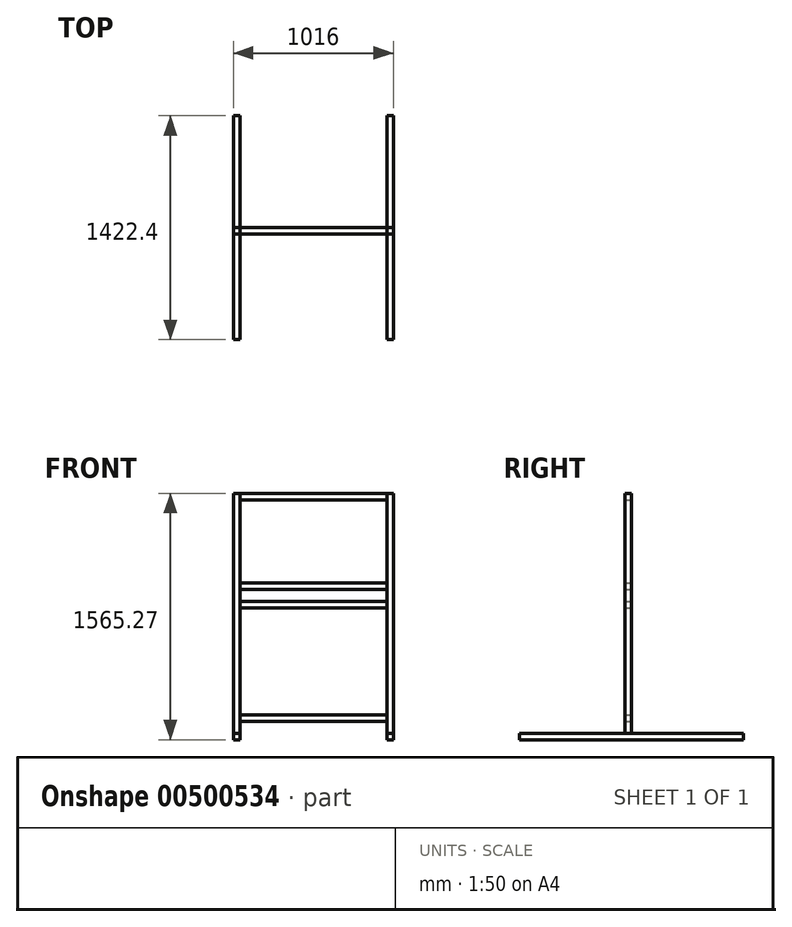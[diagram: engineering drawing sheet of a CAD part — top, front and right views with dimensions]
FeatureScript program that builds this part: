
annotation { "Feature Type Name" : "Feature", "Feature Type Description" : "" }
export const myFeature = defineFeature(function(context is Context, id is Id, definition is map)
    precondition{}
    {
        {
            var Q0;
            Q0=qCreatedBy(makeId("Front.planeOp"),FACE);
            var sketch = newSketch(context, id + "F0", { "sketchPlane" : qUnion([Q0])});
            skLineSegment(sketch, "E0", {"start": v(-508, 762) * mm, "end": v(-508, -762) * mm});
            skLineSegment(sketch, "E1", {"start": v(-508, 762) * mm, "end": v(-466.72, 762) * mm});
            skLineSegment(sketch, "E2", {"start": v(-466.72, 762) * mm, "end": v(-466.72, -762) * mm});
            skLineSegment(sketch, "E3", {"start": v(-466.72, -762) * mm, "end": v(-508, -762) * mm});
            skLineSegment(sketch, "E4.MirrorCS", {"start": v(508, 762) * mm, "end": v(466.72, 762) * mm});
            skLineSegment(sketch, "E5.MirrorCS", {"start": v(466.72, -762) * mm, "end": v(508, -762) * mm});
            skLineSegment(sketch, "E6.MirrorCS", {"start": v(508, 762) * mm, "end": v(508, -762) * mm});
            skLineSegment(sketch, "E7.MirrorCS", {"start": v(466.72, 762) * mm, "end": v(466.72, -762) * mm});
            skSolve(sketch);
        }
        {
            var Q0;
            Q0 = qSketchRegion(id + "F0", true);
            extrude(context, id + "F1", {"entities" : qUnion([Q0]), "depth" : 41.27 * mm});
        }
        {
            var Q0;
            Q0=qCreatedBy(makeId("Front.planeOp"),FACE);
            var sketch = newSketch(context, id + "F2", { "sketchPlane" : qUnion([Q0])});
            skLineSegment(sketch, "E8.0", {"start": v(-466.72, 762) * mm, "end": v(-466.72, -762) * mm, "construction": true});
            skLineSegment(sketch, "E9.0", {"start": v(466.72, 762) * mm, "end": v(466.72, -762) * mm, "construction": true});
            skLineSegment(sketch, "E10.bottom", {"start": v(-466.72, 762) * mm, "end": v(466.72, 762) * mm});
            skLineSegment(sketch, "E10.top", {"start": v(-466.72, 720.73) * mm, "end": v(466.72, 720.73) * mm});
            skLineSegment(sketch, "E10.left", {"start": v(-466.72, 762) * mm, "end": v(-466.72, 720.73) * mm});
            skLineSegment(sketch, "E10.right", {"start": v(466.72, 762) * mm, "end": v(466.72, 720.73) * mm});
            skLineSegment(sketch, "E11.bottom", {"start": v(-466.72, 193.68) * mm, "end": v(466.72, 193.68) * mm});
            skLineSegment(sketch, "E11.top", {"start": v(-466.72, 152.4) * mm, "end": v(466.72, 152.4) * mm});
            skLineSegment(sketch, "E11.left", {"start": v(-466.72, 193.68) * mm, "end": v(-466.72, 152.4) * mm});
            skLineSegment(sketch, "E11.right", {"start": v(466.72, 193.68) * mm, "end": v(466.72, 152.4) * mm});
            skLineSegment(sketch, "E12.bottom", {"start": v(-466.72, 76.2) * mm, "end": v(466.72, 76.2) * mm});
            skLineSegment(sketch, "E12.top", {"start": v(-466.72, 34.93) * mm, "end": v(466.72, 34.93) * mm});
            skLineSegment(sketch, "E12.left", {"start": v(-466.72, 76.2) * mm, "end": v(-466.72, 34.93) * mm});
            skLineSegment(sketch, "E12.right", {"start": v(466.72, 76.2) * mm, "end": v(466.72, 34.93) * mm});
            skLineSegment(sketch, "E13.bottom", {"start": v(-466.72, -644.52) * mm, "end": v(466.72, -644.52) * mm});
            skLineSegment(sketch, "E13.top", {"start": v(-466.72, -685.8) * mm, "end": v(466.72, -685.8) * mm});
            skLineSegment(sketch, "E13.left", {"start": v(-466.72, -644.52) * mm, "end": v(-466.72, -685.8) * mm});
            skLineSegment(sketch, "E13.right", {"start": v(466.72, -644.52) * mm, "end": v(466.72, -685.8) * mm});
            skSolve(sketch);
        }
        {
            var Q0;
            Q0=makeQuery(id+"F2.imprint","IMPRINT",FACE,{"disambiguationData":[TD([[makeQuery(id+"F2.imprint","IMPRINT",EDGE,{"derivedFrom":sQuery(id+"F2.wireOp",EDGE,"E10.bottom")}),-1.0]])]});
            var Q1;
            Q1=makeQuery(id+"F2.imprint","IMPRINT",FACE,{"disambiguationData":[TD([[makeQuery(id+"F2.imprint","IMPRINT",EDGE,{"derivedFrom":sQuery(id+"F2.wireOp",EDGE,"E11.bottom")}),-1.0]])]});
            var Q2;
            Q2=makeQuery(id+"F2.imprint","IMPRINT",FACE,{"disambiguationData":[TD([[makeQuery(id+"F2.imprint","IMPRINT",EDGE,{"derivedFrom":sQuery(id+"F2.wireOp",EDGE,"E12.bottom")}),-1.0]])]});
            var Q3;
            Q3=makeQuery(id+"F2.imprint","IMPRINT",FACE,{"disambiguationData":[TD([[makeQuery(id+"F2.imprint","IMPRINT",EDGE,{"derivedFrom":sQuery(id+"F2.wireOp",EDGE,"E13.bottom")}),-1.0]])]});
            extrude(context, id + "F3", {"entities" : qUnion([Q0, Q1, Q2, Q3]), "depth" : 41.27 * mm});
        }
        {
            var Q0;
            Q0=qCreatedBy(makeId("Front.planeOp"),FACE);
            var sketch = newSketch(context, id + "F4", { "sketchPlane" : qUnion([Q0])});
            skPoint(sketch, "E14.0", {"position": v(-508, -762) * mm});
            skPoint(sketch, "E15.0", {"position": v(508, -762) * mm});
            skLineSegment(sketch, "E16.bottom", {"start": v(-508, -762) * mm, "end": v(-466.72, -762) * mm});
            skLineSegment(sketch, "E16.top", {"start": v(-508, -803.28) * mm, "end": v(-466.72, -803.28) * mm});
            skLineSegment(sketch, "E16.left", {"start": v(-508, -762) * mm, "end": v(-508, -803.28) * mm});
            skLineSegment(sketch, "E16.right", {"start": v(-466.72, -762) * mm, "end": v(-466.72, -803.28) * mm});
            skLineSegment(sketch, "E17.bottom", {"start": v(508, -762) * mm, "end": v(466.72, -762) * mm});
            skLineSegment(sketch, "E17.top", {"start": v(508, -803.28) * mm, "end": v(466.72, -803.28) * mm});
            skLineSegment(sketch, "E17.left", {"start": v(508, -762) * mm, "end": v(508, -803.28) * mm});
            skLineSegment(sketch, "E17.right", {"start": v(466.72, -762) * mm, "end": v(466.72, -803.28) * mm});
            skSolve(sketch);
        }
        {
            var Q0;
            Q0=makeQuery(id+"F4.imprint","IMPRINT",FACE,{"disambiguationData":[TD([[makeQuery(id+"F4.imprint","IMPRINT",EDGE,{"derivedFrom":sQuery(id+"F4.wireOp",EDGE,"E16.bottom")}),-1.0]])]});
            var Q1;
            Q1=makeQuery(id+"F4.imprint","IMPRINT",FACE,{"disambiguationData":[TD([[makeQuery(id+"F4.imprint","IMPRINT",EDGE,{"derivedFrom":sQuery(id+"F4.wireOp",EDGE,"E17.bottom")}),1.0]])]});
            extrude(context, id + "F5", {"entities" : qUnion([Q0, Q1]), "depth" : 711.2 * mm, "hasSecondDirection" : true, "secondDirectionOppositeDirection" : true, "secondDirectionDepth" : 711.2 * mm});
        }
    });
